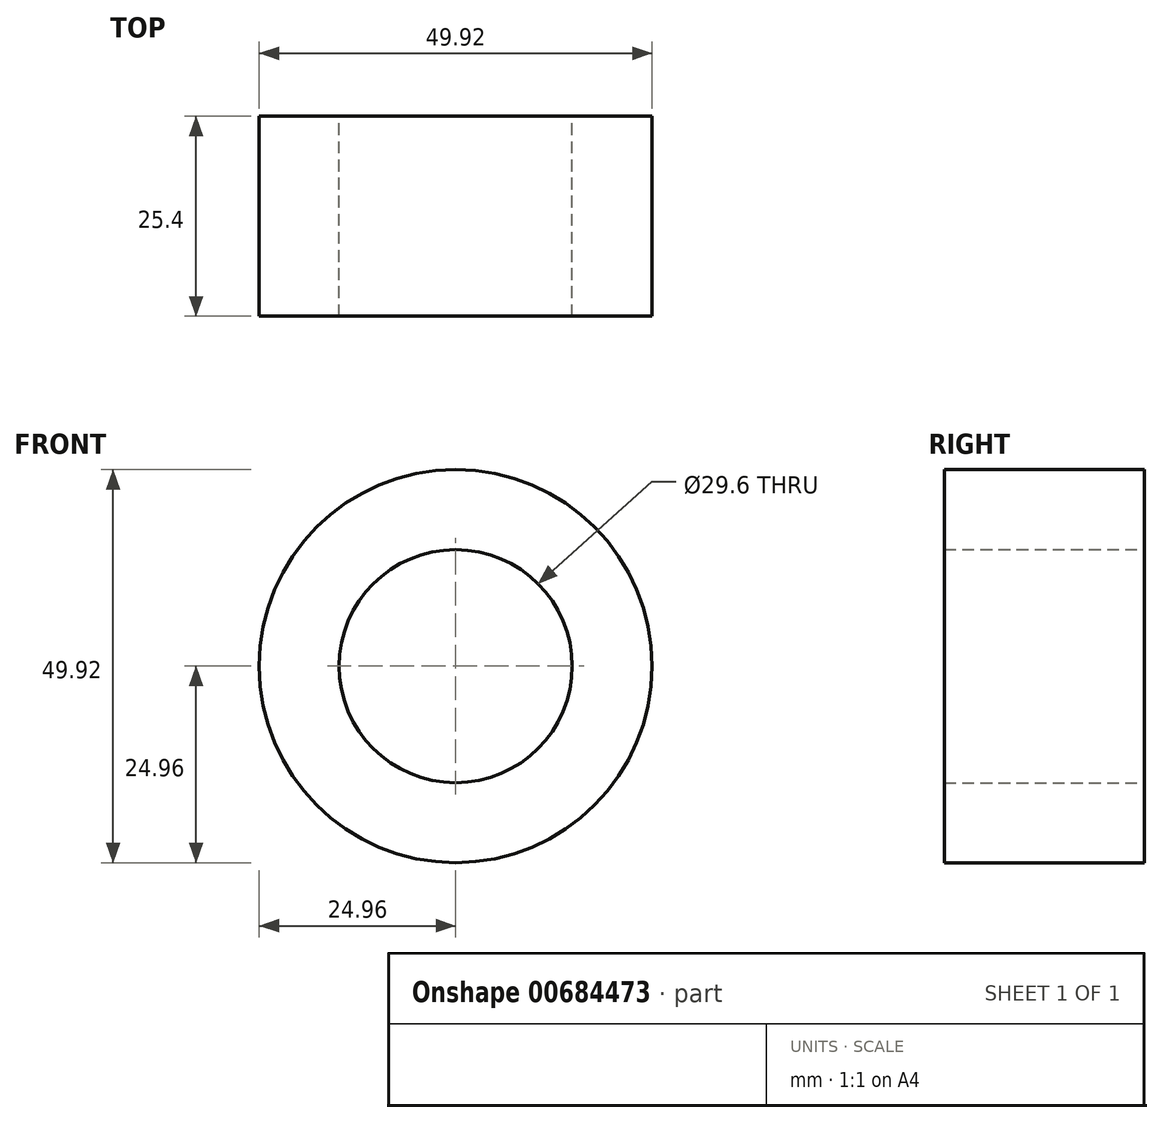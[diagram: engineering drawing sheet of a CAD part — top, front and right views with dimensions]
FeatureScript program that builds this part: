
annotation { "Feature Type Name" : "Feature", "Feature Type Description" : "" }
export const myFeature = defineFeature(function(context is Context, id is Id, definition is map)
    precondition{}
    {
        {
            var Q0;
            Q0=qCreatedBy(makeId("Front.planeOp"),FACE);
            var sketch = newSketch(context, id + "F0", { "sketchPlane" : qUnion([Q0])});
            skCircle(sketch, "E0", {"center": v(0, 0) * mm, "radius": 24.96 * mm});
            skCircle(sketch, "E1", {"center": v(0, 0) * mm, "radius": 14.8 * mm});
            skCircle(sketch, "E2", {"center": v(0, 0) * mm, "radius": 14.67 * mm});
            skSolve(sketch);
        }
        {
            var Q0;
            Q0 = qSketchRegion(id + "F0", true);
            extrude(context, id + "F1", {"entities" : qUnion([Q0]), "depth" : 25.4 * mm, "offsetDistance" : 25.4 * mm});
        }
        {
            var Q0;
            Q0=qCreatedBy(makeId("Front.planeOp"),FACE);
            var sketch = newSketch(context, id + "F2", { "sketchPlane" : qUnion([Q0])});
            skCircle(sketch, "E3", {"center": v(0, 0) * mm, "radius": 5.9 * mm});
            skCircle(sketch, "E4", {"center": v(0, 0) * mm, "radius": 2.78 * mm});
            skSolve(sketch);
        }
        {
            var Q0;
            Q0 = qSketchRegion(id + "F2", true);
            extrude(context, id + "F3", {"entities" : qUnion([Q0]), "operationType" : NewBodyOperationType.REMOVE, "oppositeDirection" : true, "depth" : 25.4 * mm, "offsetDistance" : 25.4 * mm});
        }
    });
